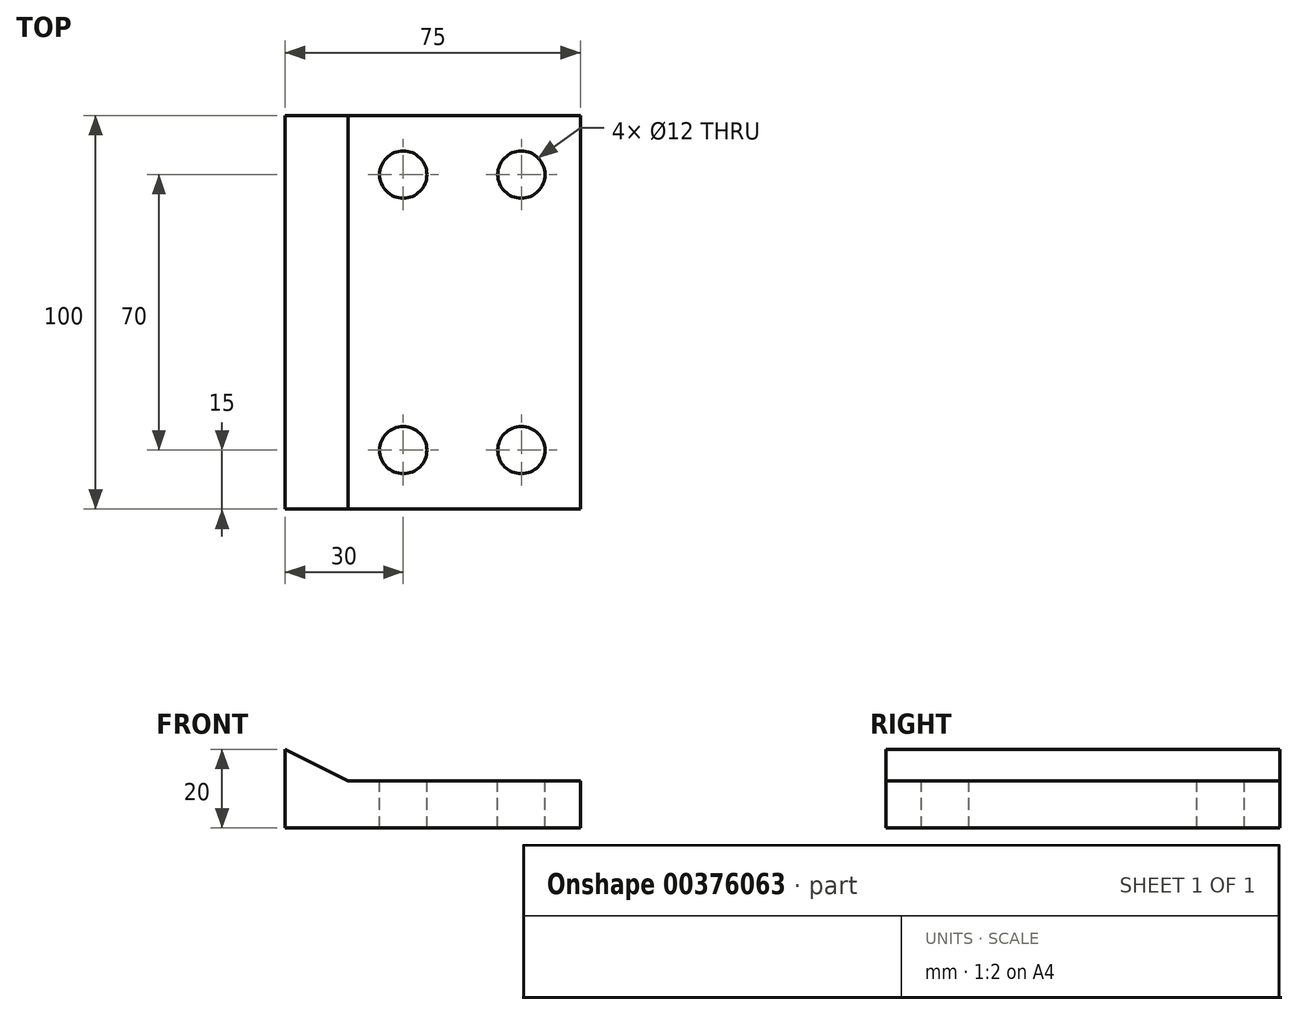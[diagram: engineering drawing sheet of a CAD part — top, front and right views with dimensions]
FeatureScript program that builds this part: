
annotation { "Feature Type Name" : "Feature", "Feature Type Description" : "" }
export const myFeature = defineFeature(function(context is Context, id is Id, definition is map)
    precondition{}
    {
        {
            var Q0;
            Q0=qCreatedBy(makeId("Top.planeOp"),FACE);
            var sketch = newSketch(context, id + "F0", { "sketchPlane" : qUnion([Q0])});
            skLineSegment(sketch, "E0.bottom", {"start": v(0, 0) * mm, "end": v(75, 0) * mm});
            skLineSegment(sketch, "E0.top", {"start": v(0, 100) * mm, "end": v(75, 100) * mm});
            skLineSegment(sketch, "E0.left", {"start": v(0, 0) * mm, "end": v(0, 100) * mm});
            skLineSegment(sketch, "E0.right", {"start": v(75, 0) * mm, "end": v(75, 100) * mm});
            skSolve(sketch);
        }
        {
            var Q0;
            Q0=makeQuery(id+"F0.imprint","IMPRINT",FACE,{"disambiguationData":[TD([[makeQuery(id+"F0.imprint","IMPRINT",EDGE,{"derivedFrom":sQuery(id+"F0.wireOp",EDGE,"E0.bottom")}),1.0]])]});
            extrude(context, id + "F1", {"entities" : qUnion([Q0]), "depth" : 12 * mm});
        }
        {
            var Q0;
            Q0=makeQuery(id+"F1.opExtrude","SWEPT_FACE",FACE,{"disambiguationData":[OSD([sQuery(id+"F0.wireOp",EDGE,"E0.bottom")])]});
            var sketch = newSketch(context, id + "F2", { "sketchPlane" : qUnion([Q0])});
            skSolve(sketch);
        }
        {
            var Q0;
            {var subQ0=sQuery(id+"F0.wireOp",EDGE,"E0.bottom");Q0=makeQuery(id+"F2.imprint","IMPRINT",FACE,{"disambiguationData":[TD([[makeQuery(id+"F2.imprint","IMPRINT",EDGE,{"derivedFrom":makeQuery(id+"F1.opExtrude","CAP_EDGE",EDGE,{"disambiguationData":[OSD([subQ0])],"isStart":true})}),1.0]])]});}
            var sketch = newSketch(context, id + "F3", { "sketchPlane" : qUnion([Q0])});
            skLineSegment(sketch, "E1", {"start": v(0, 0) * mm, "end": v(0, 12) * mm, "construction": true});
            skLineSegment(sketch, "E2", {"start": v(0, 12) * mm, "end": v(16, 12) * mm});
            skLineSegment(sketch, "E3", {"start": v(0, 12) * mm, "end": v(0, 20) * mm});
            skLineSegment(sketch, "E4", {"start": v(16, 12) * mm, "end": v(0, 20) * mm});
            skSolve(sketch);
        }
        {
            var Q0;
            Q0 = qSketchRegion(id + "F3", true);
            extrude(context, id + "F4", {"entities" : qUnion([Q0]), "operationType" : NewBodyOperationType.ADD, "oppositeDirection" : true, "depth" : 100 * mm});
        }
        {
            var Q0;
            Q0=makeQuery(id+"F1.opExtrude","CAP_FACE",FACE,{"disambiguationData":[OSD([sQuery(id+"F0.wireOp",EDGE,"E0.bottom"),sQuery(id+"F0.wireOp",EDGE,"E0.top"),sQuery(id+"F0.wireOp",EDGE,"E0.left"),sQuery(id+"F0.wireOp",EDGE,"E0.right")])],"isStart":false});
            var sketch = newSketch(context, id + "F5", { "sketchPlane" : qUnion([Q0])});
            skLineSegment(sketch, "E5", {"start": v(75, 0) * mm, "end": v(60, 0) * mm, "construction": true});
            skLineSegment(sketch, "E6", {"start": v(60, 0) * mm, "end": v(45, 0) * mm, "construction": true});
            skLineSegment(sketch, "E7", {"start": v(45, 0) * mm, "end": v(30, 0) * mm, "construction": true});
            skLineSegment(sketch, "E8", {"start": v(30, 0) * mm, "end": v(30, 15) * mm, "construction": true});
            skLineSegment(sketch, "E9", {"start": v(60, 0) * mm, "end": v(60, 15) * mm, "construction": true});
            skLineSegment(sketch, "E10", {"start": v(75, 50) * mm, "end": v(16, 50) * mm, "construction": true});
            skLineSegment(sketch, "E11.MirrorCS", {"start": v(30, 100) * mm, "end": v(30, 85) * mm, "construction": true});
            skLineSegment(sketch, "E12.MirrorCS", {"start": v(60, 100) * mm, "end": v(60, 85) * mm, "construction": true});
            skSolve(sketch);
        }
        {
            var Q0;
            Q0=sQuery(id+"F5.wireOp",VERTEX,"E8.end");
            var Q1;
            Q1=sQuery(id+"F5.wireOp",VERTEX,"E9.end");
            var Q2;
            Q2=sQuery(id+"F5.wireOp",VERTEX,"E12.MirrorCS.end");
            var Q3;
            Q3=sQuery(id+"F5.wireOp",VERTEX,"E11.MirrorCS.end");
            var Q4;
            Q4=makeQuery(id+"F1.opExtrude","SWEPT_BODY",BODY,{"disambiguationData":[OSD([sQuery(id+"F0.wireOp",EDGE,"E0.bottom"),sQuery(id+"F0.wireOp",EDGE,"E0.top"),sQuery(id+"F0.wireOp",EDGE,"E0.left"),sQuery(id+"F0.wireOp",EDGE,"E0.right")])]});
            hole(context, id + "F6", {"style" : HoleStyle.SIMPLE, "endStyle" : HoleEndStyle.BLIND, "holeDiameter" : 12 * mm, "holeDepth" : 12 * mm, "isTappedThrough" : true, "tappedDepth" : 12 * mm, "tapClearance" : 3, "locations" : qUnion([Q0, Q1, Q2, Q3]), "scope" : qUnion([Q4])});
        }
    });
